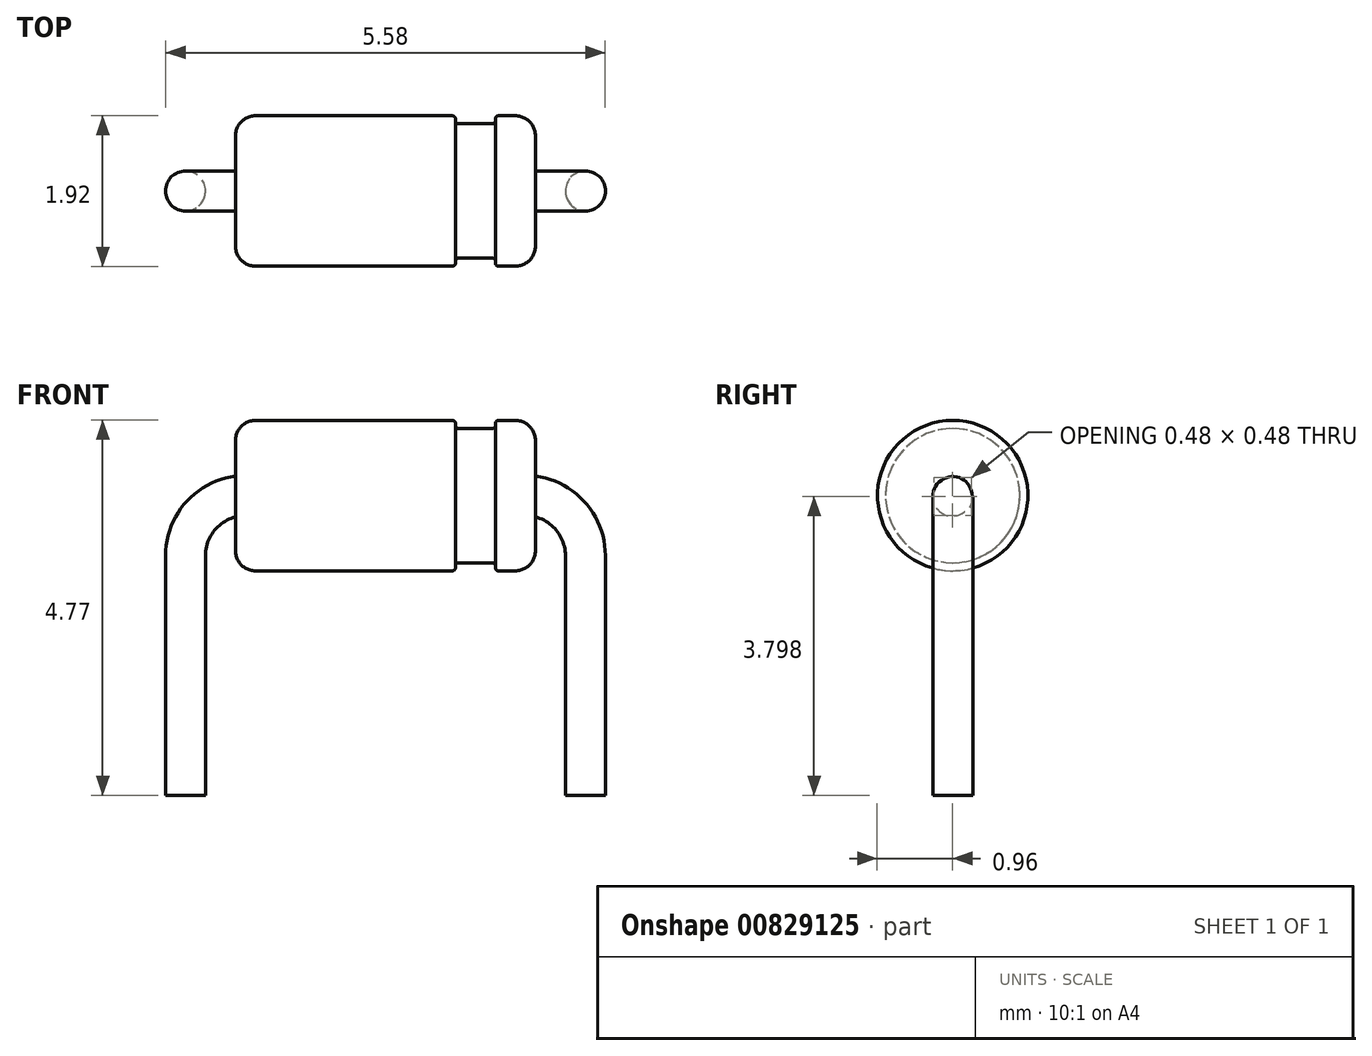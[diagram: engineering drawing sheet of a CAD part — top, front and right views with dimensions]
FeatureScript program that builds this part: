
annotation { "Feature Type Name" : "Feature", "Feature Type Description" : "" }
export const myFeature = defineFeature(function(context is Context, id is Id, definition is map)
    precondition{}
    {
        {
            var Q0;
            Q0=qCreatedBy(makeId("Front.planeOp"),FACE);
            var sketch = newSketch(context, id + "F0", { "sketchPlane" : qUnion([Q0])});
            skLineSegment(sketch, "E0.bottom", {"start": v(-1.9, 0) * mm, "end": v(1.9, 0) * mm});
            skLineSegment(sketch, "E0.top", {"start": v(-1.9, 0.96) * mm, "end": v(0.89, 0.96) * mm});
            skLineSegment(sketch, "E0.left", {"start": v(-1.9, 0) * mm, "end": v(-1.9, 0.96) * mm});
            skLineSegment(sketch, "E0.right", {"start": v(1.9, 0) * mm, "end": v(1.9, 0.96) * mm});
            skLineSegment(sketch, "E1", {"start": v(0.89, 0.96) * mm, "end": v(0.89, 0.85) * mm});
            skLineSegment(sketch, "E2", {"start": v(0.89, 0.85) * mm, "end": v(1.4, 0.85) * mm});
            skLineSegment(sketch, "E3", {"start": v(1.4, 0.85) * mm, "end": v(1.4, 0.96) * mm});
            skLineSegment(sketch, "E4.trimOffspring", {"start": v(1.4, 0.96) * mm, "end": v(1.9, 0.96) * mm});
            skSolve(sketch);
        }
        {
            var Q0;
            Q0 = qSketchRegion(id + "F0", true);
            var Q1;
            Q1=sQuery(id+"F0.wireOp",EDGE,"E0.bottom");
            revolve(context, id + "F1", {"surfaceOperationType" : NewSurfaceOperationType.NEW, "entities" : qUnion([Q0]), "axis" : qUnion([Q1]), "revolveType" : RevolveType.FULL});
        }
        {
            var Q0;
            Q0=makeQuery(id+"F1.opRevolve","SWEPT_EDGE",EDGE,{"disambiguationData":[OSD([sQuery(id+"F0.wireOp",EDGE,"E0.right"),sQuery(id+"F0.wireOp",EDGE,"E4.trimOffspring")])]});
            var Q1;
            Q1=makeQuery(id+"F1.opRevolve","SWEPT_EDGE",EDGE,{"disambiguationData":[OSD([sQuery(id+"F0.wireOp",EDGE,"E0.top"),sQuery(id+"F0.wireOp",EDGE,"E0.left")])]});
            fillet(context, id + "F2", {"entities" : qUnion([Q0, Q1]), "radius" : 0.25 * mm, "tangentPropagation" : true, "allowEdgeOverflow" : false});
        }
        {
            var Q0;
            Q0=makeQuery(id+"F1.opRevolve","SWEPT_EDGE",EDGE,{"disambiguationData":[OSD([sQuery(id+"F0.wireOp",EDGE,"E3"),sQuery(id+"F0.wireOp",EDGE,"E4.trimOffspring")])]});
            var Q1;
            Q1=makeQuery(id+"F1.opRevolve","SWEPT_EDGE",EDGE,{"disambiguationData":[OSD([sQuery(id+"F0.wireOp",EDGE,"E2"),sQuery(id+"F0.wireOp",EDGE,"E3")])]});
            var Q2;
            Q2=makeQuery(id+"F1.opRevolve","SWEPT_EDGE",EDGE,{"disambiguationData":[OSD([sQuery(id+"F0.wireOp",EDGE,"E1"),sQuery(id+"F0.wireOp",EDGE,"E2")])]});
            var Q3;
            Q3=makeQuery(id+"F1.opRevolve","SWEPT_EDGE",EDGE,{"disambiguationData":[OSD([sQuery(id+"F0.wireOp",EDGE,"E0.top"),sQuery(id+"F0.wireOp",EDGE,"E1")])]});
            fillet(context, id + "F3", {"entities" : qUnion([Q0, Q1, Q2, Q3]), "radius" : 0.04 * mm, "tangentPropagation" : true, "allowEdgeOverflow" : false});
        }
        {
            var Q0;
            Q0=qCreatedBy(makeId("Front.planeOp"),FACE);
            var sketch = newSketch(context, id + "F4", { "sketchPlane" : qUnion([Q0])});
            skLineSegment(sketch, "E5", {"start": v(-1.78, 0) * mm, "end": v(1.78, 0) * mm});
            skLineSegment(sketch, "E6", {"start": v(2.54, -0.76) * mm, "end": v(2.54, -3.81) * mm});
            skLineSegment(sketch, "E7", {"start": v(-2.54, -0.76) * mm, "end": v(-2.54, -3.81) * mm});
            skLineSegment(sketch, "E8", {"start": v(-2.54, -3.81) * mm, "end": v(2.54, -3.81) * mm, "construction": true});
            skPoint(sketch, "E9.visualSharp", {"position": v(-2.54, 0) * mm});
            skArc(sketch, "E9.filletArc", {"start": v(-1.78, 0) * mm, "mid": v(-2.32, -0.22) * mm, "end": v(-2.54, -0.76) * mm});
            skPoint(sketch, "E10.visualSharp", {"position": v(2.54, 0) * mm});
            skArc(sketch, "E10.filletArc", {"start": v(2.54, -0.76) * mm, "mid": v(2.32, -0.22) * mm, "end": v(1.78, 0) * mm});
            skSolve(sketch);
        }
        {
            var Q0;
            Q0=qCreatedBy(makeId("Top.planeOp"),FACE);
            cPlane(context, id + "F5", {"entities" : qUnion([Q0]), "cplaneType" : CPlaneType.OFFSET, "offset" : 3.8 * mm, "oppositeDirection" : true, "width" : 152.4 * mm, "height" : 152.4 * mm});
        }
        {
            var Q0;
            Q0=qCreatedBy(id+"F5.planeOp",FACE);
            var sketch = newSketch(context, id + "F6", { "sketchPlane" : qUnion([Q0])});
            skCircle(sketch, "E11", {"center": v(-2.54, 0) * mm, "radius": 0.25 * mm});
            skSolve(sketch);
        }
        {
            var Q0;
            Q0=makeQuery(id+"F6.imprint","IMPRINT",FACE,{"disambiguationData":[TD([[makeQuery(id+"F6.imprint","IMPRINT",EDGE,{"derivedFrom":sQuery(id+"F6.wireOp",EDGE,"E11")}),1.0]])]});
            var Q1;
            Q1=sQuery(id+"F4.wireOp",EDGE,"E7");
            var Q2;
            Q2=sQuery(id+"F4.wireOp",EDGE,"E9.filletArc");
            var Q3;
            Q3=sQuery(id+"F4.wireOp",EDGE,"E5");
            var Q4;
            Q4=sQuery(id+"F4.wireOp",EDGE,"E10.filletArc");
            var Q5;
            Q5=sQuery(id+"F4.wireOp",EDGE,"E6");
            sweep(context, id + "F7", {"operationType" : NewBodyOperationType.ADD, "profiles" : qUnion([Q0]), "path" : qUnion([Q1, Q2, Q3, Q4, Q5])});
        }
    });
